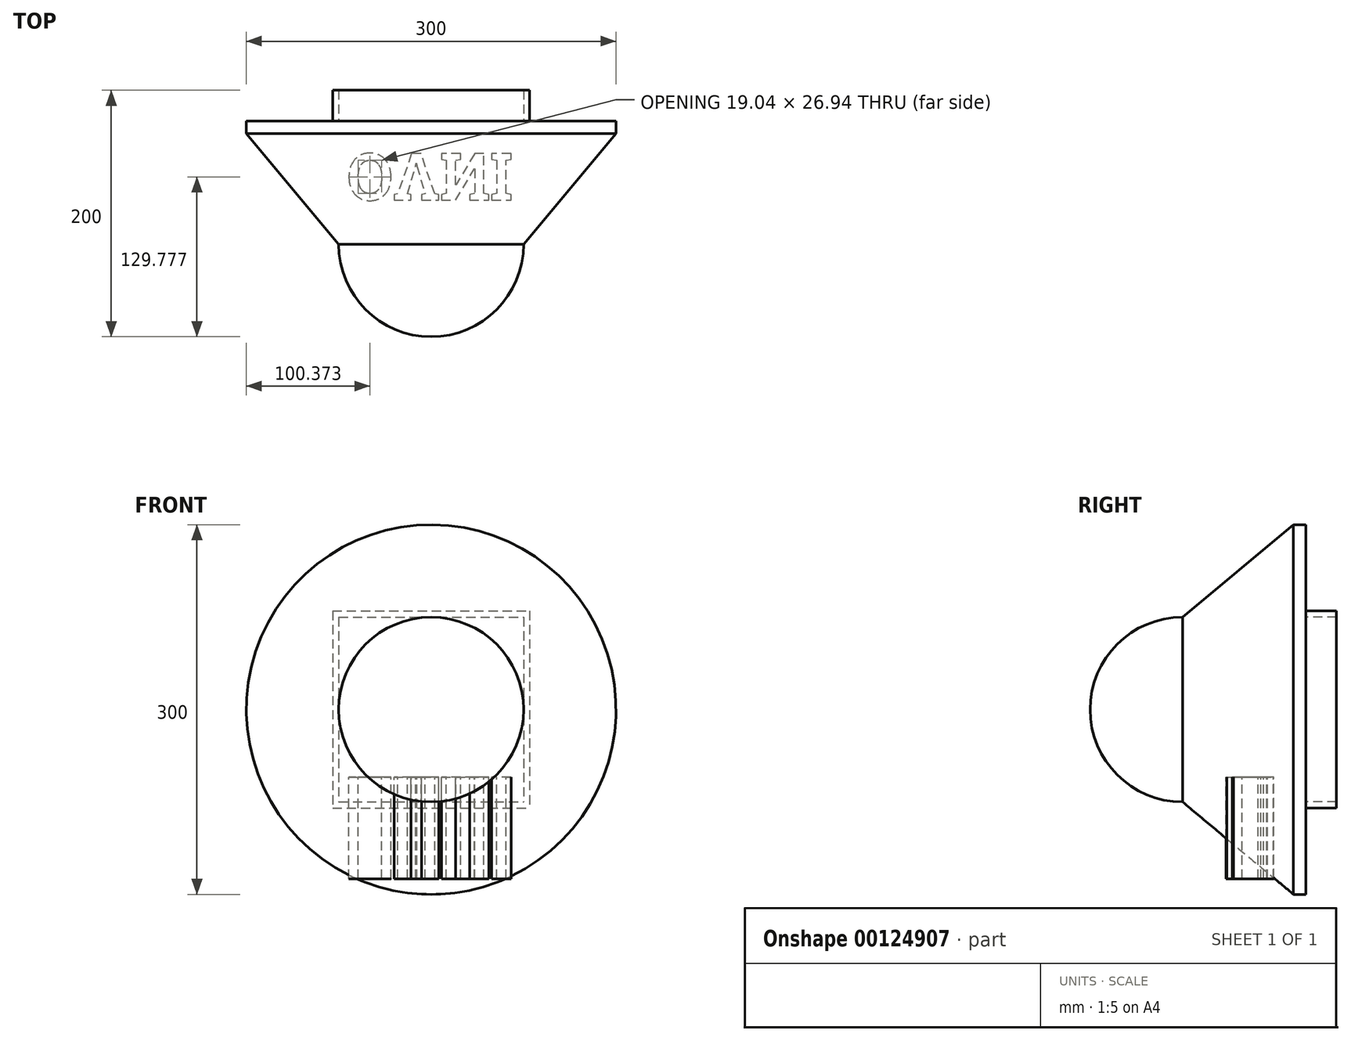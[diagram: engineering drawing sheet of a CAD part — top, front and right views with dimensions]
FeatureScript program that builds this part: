
annotation { "Feature Type Name" : "Feature", "Feature Type Description" : "" }
export const myFeature = defineFeature(function(context is Context, id is Id, definition is map)
    precondition{}
    {
        {
            var Q0;
            Q0=qCreatedBy(makeId("Front.planeOp"),FACE);
            var sketch = newSketch(context, id + "F0", { "sketchPlane" : qUnion([Q0])});
            skLineSegment(sketch, "E0.bottom", {"start": v(-80, 80) * mm, "end": v(80, 80) * mm});
            skLineSegment(sketch, "E0.top", {"start": v(-80, -80) * mm, "end": v(80, -80) * mm});
            skLineSegment(sketch, "E0.left", {"start": v(-80, 80) * mm, "end": v(-80, -80) * mm});
            skLineSegment(sketch, "E0.right", {"start": v(80, 80) * mm, "end": v(80, -80) * mm});
            skSolve(sketch);
        }
        {
            var Q0;
            Q0 = qSketchRegion(id + "F0", true);
            extrude(context, id + "F1", {"entities" : qUnion([Q0]), "depth" : 25 * mm});
        }
        {
            var Q0;
            Q0=makeQuery(id+"F1.opExtrude","CAP_FACE",FACE,{"disambiguationData":[OSD([sQuery(id+"F0.wireOp",EDGE,"E0.bottom"),sQuery(id+"F0.wireOp",EDGE,"E0.top"),sQuery(id+"F0.wireOp",EDGE,"E0.left"),sQuery(id+"F0.wireOp",EDGE,"E0.right")])],"isStart":false});
            var sketch = newSketch(context, id + "F2", { "sketchPlane" : qUnion([Q0])});
            skLineSegment(sketch, "E1.bottom", {"start": v(-75, 75) * mm, "end": v(75, 75) * mm});
            skLineSegment(sketch, "E1.top", {"start": v(-75, -75) * mm, "end": v(75, -75) * mm});
            skLineSegment(sketch, "E1.left", {"start": v(-75, 75) * mm, "end": v(-75, -75) * mm});
            skLineSegment(sketch, "E1.right", {"start": v(75, 75) * mm, "end": v(75, -75) * mm});
            skSolve(sketch);
        }
        {
            var Q0;
            Q0=makeQuery(id+"F2.imprint","IMPRINT",FACE,{"disambiguationData":[TD([[makeQuery(id+"F2.imprint","IMPRINT",EDGE,{"derivedFrom":sQuery(id+"F2.wireOp",EDGE,"E1.bottom")}),-1.0]])]});
            extrude(context, id + "F3", {"entities" : qUnion([Q0]), "operationType" : NewBodyOperationType.REMOVE, "oppositeDirection" : true, "depth" : 30 * mm});
        }
        {
            var Q0;
            Q0=makeQuery(id+"F1.opExtrude","CAP_FACE",FACE,{"disambiguationData":[OSD([sQuery(id+"F0.wireOp",EDGE,"E0.bottom"),sQuery(id+"F0.wireOp",EDGE,"E0.top"),sQuery(id+"F0.wireOp",EDGE,"E0.left"),sQuery(id+"F0.wireOp",EDGE,"E0.right")])],"isStart":false});
            var sketch = newSketch(context, id + "F4", { "sketchPlane" : qUnion([Q0])});
            skCircle(sketch, "E2", {"center": v(0, 0) * mm, "radius": 150 * mm});
            skSolve(sketch);
        }
        {
            var Q0;
            Q0=makeQuery(id+"F4.imprint","IMPRINT",FACE,{"disambiguationData":[TD([[makeQuery(id+"F4.imprint","IMPRINT",EDGE,{"derivedFrom":sQuery(id+"F4.wireOp",EDGE,"E2")}),1.0]])]});
            cPlane(context, id + "F5", {"entities" : qUnion([Q0]), "cplaneType" : CPlaneType.OFFSET, "offset" : 100 * mm, "width" : 150 * mm, "height" : 150 * mm});
        }
        {
            var Q0;
            Q0=qCreatedBy(id+"F5.planeOp",FACE);
            var sketch = newSketch(context, id + "F6", { "sketchPlane" : qUnion([Q0])});
            skCircle(sketch, "E3", {"center": v(0, 0) * mm, "radius": 75 * mm});
            skSolve(sketch);
        }
        {
            var Q0;
            Q0 = qSketchRegion(id + "F4", true);
            extrude(context, id + "F7", {"entities" : qUnion([Q0]), "operationType" : NewBodyOperationType.ADD, "depth" : 10 * mm});
        }
        {
            var Q1;
            Q1=makeQuery(id+"F7.opExtrude","CAP_FACE",FACE,{"disambiguationData":[OSD([sQuery(id+"F4.wireOp",EDGE,"E2")])],"isStart":false});
            var Q2;
            Q2=makeQuery(id+"F6.imprint","IMPRINT",FACE,{"disambiguationData":[TD([[makeQuery(id+"F6.imprint","IMPRINT",EDGE,{"derivedFrom":sQuery(id+"F6.wireOp",EDGE,"E3")}),1.0]])]});
            loft(context, id + "F8", {"operationType" : NewBodyOperationType.ADD, "sheetProfilesArray" : [{ "sheetProfileEntities" : qUnion([Q1]) }, { "sheetProfileEntities" : qUnion([Q2]) }]});
        }
        {
            var Q0;
            Q0=makeQuery(id+"F8.opLoft","CAP_FACE",FACE,{"disambiguationData":[OSD([makeQuery(id+"F6.imprint","IMPRINT",FACE,{"disambiguationData":[TD([[makeQuery(id+"F6.imprint","IMPRINT",EDGE,{"derivedFrom":sQuery(id+"F6.wireOp",EDGE,"E3")}),1.0]])]})])],"isStart":true});
            var sketch = newSketch(context, id + "F9", { "sketchPlane" : qUnion([Q0])});
            skLineSegment(sketch, "E4", {"start": v(-75, 0) * mm, "end": v(75, 0) * mm});
            skSolve(sketch);
        }
        {
            var Q0;
            {var subQ0=sQuery(id+"F9.wireOp",EDGE,"E4");Q0=makeQuery(id+"F9.imprint","IMPRINT",FACE,{"disambiguationData":[TD([[makeQuery(id+"F9.imprint","IMPRINT",EDGE,{"derivedFrom":subQ0}),1.0]])]});}
            var Q1;
            Q1=sQuery(id+"F9.wireOp",EDGE,"E4");
            revolve(context, id + "F10", {"operationType" : NewBodyOperationType.ADD, "entities" : qUnion([Q0]), "axis" : qUnion([Q1]), "revolveType" : RevolveType.TWO_DIRECTIONS, "angle" : 90 * degree, "angleBack" : 90 * degree});
        }
        {
            var Q0;
            Q0=makeQuery(id+"F1.opExtrude","SWEPT_FACE",FACE,{"disambiguationData":[OSD([sQuery(id+"F0.wireOp",EDGE,"E0.top")])]});
            var sketch = newSketch(context, id + "F11", { "sketchPlane" : qUnion([Q0])});
            skText(sketch, "E5", { "text": "OVNI", "fontName": "RobotoSlab-Bold.ttf"});
            const initialGuessF11  = {"E5": [-0.09342, 0.05143, 1, 0, 0.03809]};
            skSetInitialGuess(sketch, initialGuessF11);
            skSolve(sketch);
        }
        {
            var Q0;
            Q0 = qSketchRegion(id + "F11", true);
            extrude(context, id + "F12", {"entities" : qUnion([Q0]), "depth" : 82.35 * mm});
        }
        {
            var Q0;
            Q0=makeQuery(id+"F12.opExtrude","SWEPT_BODY",BODY,{"disambiguationData":[OSD([sQuery(id+"F11.wireOp",EDGE,"E5.sketch_text.stroke-62"),sQuery(id+"F11.wireOp",EDGE,"E5.sketch_text.stroke-63"),sQuery(id+"F11.wireOp",EDGE,"E5.sketch_text.stroke-64"),sQuery(id+"F11.wireOp",EDGE,"E5.sketch_text.stroke-65"),sQuery(id+"F11.wireOp",EDGE,"E5.sketch_text.stroke-66"),sQuery(id+"F11.wireOp",EDGE,"E5.sketch_text.stroke-67"),sQuery(id+"F11.wireOp",EDGE,"E5.sketch_text.stroke-68"),sQuery(id+"F11.wireOp",EDGE,"E5.sketch_text.stroke-69"),sQuery(id+"F11.wireOp",EDGE,"E5.sketch_text.stroke-70"),sQuery(id+"F11.wireOp",EDGE,"E5.sketch_text.stroke-71"),sQuery(id+"F11.wireOp",EDGE,"E5.sketch_text.stroke-72"),sQuery(id+"F11.wireOp",EDGE,"E5.sketch_text.stroke-73")])]});
            var Q1;
            Q1=makeQuery(id+"F12.opExtrude","SWEPT_BODY",BODY,{"disambiguationData":[OSD([sQuery(id+"F11.wireOp",EDGE,"E5.sketch_text.stroke-38"),sQuery(id+"F11.wireOp",EDGE,"E5.sketch_text.stroke-39"),sQuery(id+"F11.wireOp",EDGE,"E5.sketch_text.stroke-40"),sQuery(id+"F11.wireOp",EDGE,"E5.sketch_text.stroke-41"),sQuery(id+"F11.wireOp",EDGE,"E5.sketch_text.stroke-42"),sQuery(id+"F11.wireOp",EDGE,"E5.sketch_text.stroke-43"),sQuery(id+"F11.wireOp",EDGE,"E5.sketch_text.stroke-44"),sQuery(id+"F11.wireOp",EDGE,"E5.sketch_text.stroke-45"),sQuery(id+"F11.wireOp",EDGE,"E5.sketch_text.stroke-46"),sQuery(id+"F11.wireOp",EDGE,"E5.sketch_text.stroke-47"),sQuery(id+"F11.wireOp",EDGE,"E5.sketch_text.stroke-48"),sQuery(id+"F11.wireOp",EDGE,"E5.sketch_text.stroke-49"),sQuery(id+"F11.wireOp",EDGE,"E5.sketch_text.stroke-50"),sQuery(id+"F11.wireOp",EDGE,"E5.sketch_text.stroke-51"),sQuery(id+"F11.wireOp",EDGE,"E5.sketch_text.stroke-52"),sQuery(id+"F11.wireOp",EDGE,"E5.sketch_text.stroke-53"),sQuery(id+"F11.wireOp",EDGE,"E5.sketch_text.stroke-54"),sQuery(id+"F11.wireOp",EDGE,"E5.sketch_text.stroke-55"),sQuery(id+"F11.wireOp",EDGE,"E5.sketch_text.stroke-56"),sQuery(id+"F11.wireOp",EDGE,"E5.sketch_text.stroke-57"),sQuery(id+"F11.wireOp",EDGE,"E5.sketch_text.stroke-58"),sQuery(id+"F11.wireOp",EDGE,"E5.sketch_text.stroke-59"),sQuery(id+"F11.wireOp",EDGE,"E5.sketch_text.stroke-60"),sQuery(id+"F11.wireOp",EDGE,"E5.sketch_text.stroke-61")])]});
            var Q2;
            Q2=makeQuery(id+"F12.opExtrude","SWEPT_BODY",BODY,{"disambiguationData":[OSD([sQuery(id+"F11.wireOp",EDGE,"E5.sketch_text.stroke-20"),sQuery(id+"F11.wireOp",EDGE,"E5.sketch_text.stroke-21"),sQuery(id+"F11.wireOp",EDGE,"E5.sketch_text.stroke-22"),sQuery(id+"F11.wireOp",EDGE,"E5.sketch_text.stroke-23"),sQuery(id+"F11.wireOp",EDGE,"E5.sketch_text.stroke-24"),sQuery(id+"F11.wireOp",EDGE,"E5.sketch_text.stroke-25"),sQuery(id+"F11.wireOp",EDGE,"E5.sketch_text.stroke-26"),sQuery(id+"F11.wireOp",EDGE,"E5.sketch_text.stroke-27"),sQuery(id+"F11.wireOp",EDGE,"E5.sketch_text.stroke-28"),sQuery(id+"F11.wireOp",EDGE,"E5.sketch_text.stroke-29"),sQuery(id+"F11.wireOp",EDGE,"E5.sketch_text.stroke-30"),sQuery(id+"F11.wireOp",EDGE,"E5.sketch_text.stroke-31"),sQuery(id+"F11.wireOp",EDGE,"E5.sketch_text.stroke-32"),sQuery(id+"F11.wireOp",EDGE,"E5.sketch_text.stroke-33"),sQuery(id+"F11.wireOp",EDGE,"E5.sketch_text.stroke-34"),sQuery(id+"F11.wireOp",EDGE,"E5.sketch_text.stroke-35"),sQuery(id+"F11.wireOp",EDGE,"E5.sketch_text.stroke-36"),sQuery(id+"F11.wireOp",EDGE,"E5.sketch_text.stroke-37")])]});
            var Q3;
            Q3=makeQuery(id+"F12.opExtrude","SWEPT_BODY",BODY,{"disambiguationData":[OSD([sQuery(id+"F11.wireOp",EDGE,"E5.sketch_text.stroke-0"),sQuery(id+"F11.wireOp",EDGE,"E5.sketch_text.stroke-1"),sQuery(id+"F11.wireOp",EDGE,"E5.sketch_text.stroke-2"),sQuery(id+"F11.wireOp",EDGE,"E5.sketch_text.stroke-3"),sQuery(id+"F11.wireOp",EDGE,"E5.sketch_text.stroke-4"),sQuery(id+"F11.wireOp",EDGE,"E5.sketch_text.stroke-5"),sQuery(id+"F11.wireOp",EDGE,"E5.sketch_text.stroke-6"),sQuery(id+"F11.wireOp",EDGE,"E5.sketch_text.stroke-7"),sQuery(id+"F11.wireOp",EDGE,"E5.sketch_text.stroke-8"),sQuery(id+"F11.wireOp",EDGE,"E5.sketch_text.stroke-9"),sQuery(id+"F11.wireOp",EDGE,"E5.sketch_text.stroke-10"),sQuery(id+"F11.wireOp",EDGE,"E5.sketch_text.stroke-11"),sQuery(id+"F11.wireOp",EDGE,"E5.sketch_text.stroke-12"),sQuery(id+"F11.wireOp",EDGE,"E5.sketch_text.stroke-13"),sQuery(id+"F11.wireOp",EDGE,"E5.sketch_text.stroke-14"),sQuery(id+"F11.wireOp",EDGE,"E5.sketch_text.stroke-15"),sQuery(id+"F11.wireOp",EDGE,"E5.sketch_text.stroke-16"),sQuery(id+"F11.wireOp",EDGE,"E5.sketch_text.stroke-17"),sQuery(id+"F11.wireOp",EDGE,"E5.sketch_text.stroke-18"),sQuery(id+"F11.wireOp",EDGE,"E5.sketch_text.stroke-19")])]});
            transform(context, id + "F13", {"entities" : qUnion([Q0, Q1, Q2, Q3]), "transformType" : TransformType.TRANSLATION_3D, "dx" : 25 * mm, "dy" : 0 * mm, "dz" : 25 * mm, "makeCopy" : false});
        }
    });
